# Revit family: Furniture-Wall_Mount-Vanity-KOHLER-Spacity-K-32162T_1
name_source: partatom
category: Casework
units: mm (PartAtom-declared; Revit-internal decimal feet)

## family parameters
Cut with Voids When Loaded = No
Host = Face
OmniClass Number = 23.21.19.15.33
OmniClass Title = Residential Specialty Casework
Room Calculation Point = No
Shared = No

## types (2) — shared parameters
ADA Compliant = No
Assembly Code = E2010.30
Construction Type = Wall Mount
Date Modified = 10/06/2022
Default Elevation = 35"
Depth = 17 7/16"
Description = 750MM 30 Inch Bathroom Vanity with Open Drawer And Power Socket
Hardware Included = No
Height = 24 5/8"
Manufacturer = Kohler Co.
Master Format 2014 = 12 35 30.23
Master Format 2014 Name = Bathroom Casework
Material = Solid Wood Construction
Product Name = Spacity
URL = http://www.kohler.com.cn
WaterSense Certified = No
Width = 28 13/16"

## per-type parameters (varying)
| type | Model | Product Finish | Secondary Finish | Type |
| PPW-White | K-32162T-PPW | KOHLER-Wood-PPW-White | KOHLER-Melamine-MRL | 1 |
| PPG-Black | K-32162T-PPG | KOHLER-Wood-PPG-Black | KOHLER-Melamine-MRH | 2 |

note: column(s) folded — value = type name in every type: Finish

## geometry (parser evidence)
native form markers: Sweep x4
no freeform markers — native parametric forms only
